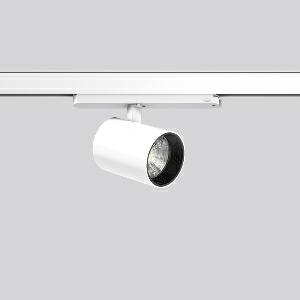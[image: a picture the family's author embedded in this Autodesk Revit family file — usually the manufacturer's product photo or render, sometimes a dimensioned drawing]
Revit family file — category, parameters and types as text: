
# Revit family: deecos_s_mini_track-in_742253_002_2_22a1
name_source: partatom
category: Lighting Fixtures
units: mm (PartAtom-declared; Revit-internal decimal feet)

## family parameters
Cut with Voids When Loaded = No
Host = Face
Light Source = No
Part Type = Normal
Room Calculation Point = No
Round Connector Dimension = Use Diameter
Shared = No

## types (1)
- DEECOS S mini track-in (1 x LED Modul 927, 2100 lm, 2700)
    Apparent Load = 20 VA
    Approval mark = CE
    CIE Flux Codes = 99 100 100 100 100
    Color Rendering = 92
    Color Temperature = 2700
    Default Elevation = 1800 mm
    Description = Series: DEECOS S mini track-in
LED surface-mounted projector in modern design with no visible cooling ribs. Housing: die-cast aluminium, powder-coated. Rotation range: 356°. Swivel range: 90°. Black plastic ring and recessed LED to prevent glare from the side. Optical assembly with lens made of plastic (polycarbonate) for the best homogeneous light distribution - can be changed without tools. Best colour rendering index Ra>90. With multi adaptor for 3-circuit tracks 230 V. Suitable for Track on ceiling, Wall track. Track-in driver integrated into the adapter. High quality converter without flickering and stroboscopic effect. The following accessories can be mounted without use of tools: interchangeable lenses, decorative glasses, honeycomb louvre, clear and frosted diffusers, white interchangeable plastic ring. 
Colour: traffic white, matt (RAL 9016)
Diameter: 87 mm
Height: 135 mm
Lamp: LED
Socket: without socket
Colour temperature: 2700K
Colour rendering index (CRI): 92
System power: 20 W
Rated luminous flux: 2100 lm
Luminous efficiency: 105 lm/W
Control gear: Regulated power supply
Protection class: II
Type of protection: IP 20
    Height = 135 mm
    Lamp = 1 x LED Modul 927
    Lamp Light Flux = 2100 lm
    Lamp count = 1
    Length = 87 mm
    Lifetime = 50000 h
    Luminous efficacy = 105 lm/W
    Manufacturer = RZB
    ModVariant = No
    Model = 742253.002.2
    Mounting Place = Ceiling
    Mounting Type = Rail mounted
    Number of Poles = 1
    OnlyDefault = Yes
    Power Factor = 1
    Product Name = DEECOS S mini track-in
    Product group = Track mounted projectors
    ProductGroupID = 301
    Protection Class = Protection class II
    Protection Degree = IP 20
    RLX_Detail_Level = 1
    RLX_Emergency_Light_Flux = 0 lm
    RLX_Emergency_Type = 0
    RLX_Emergency_Type_DB = No
    RlxData = <blob elided: 34893 chars, md5=e22dd327>
    Socket = socket
    Standby Power = 0 W
    System Light Flux = 2100 lm
    System Power = 20 W
    Type Comments = Product without accessories
    Type Image = 742108.002.jpg
    URL = http://relux.com
    VarID = ---
    Voltage = 230 V
    Voltage Range = 220-240 V
    Weight = 0.00 kg
    Width = 0 mm  [stored 0 ft]

note: [stored X ft] marks values corroborated as IEEE doubles in the binary element streams (Revit-internal decimal feet)

## geometry (parser evidence)
native form markers: Blend x4, Sweep x11
no freeform markers — native parametric forms only
